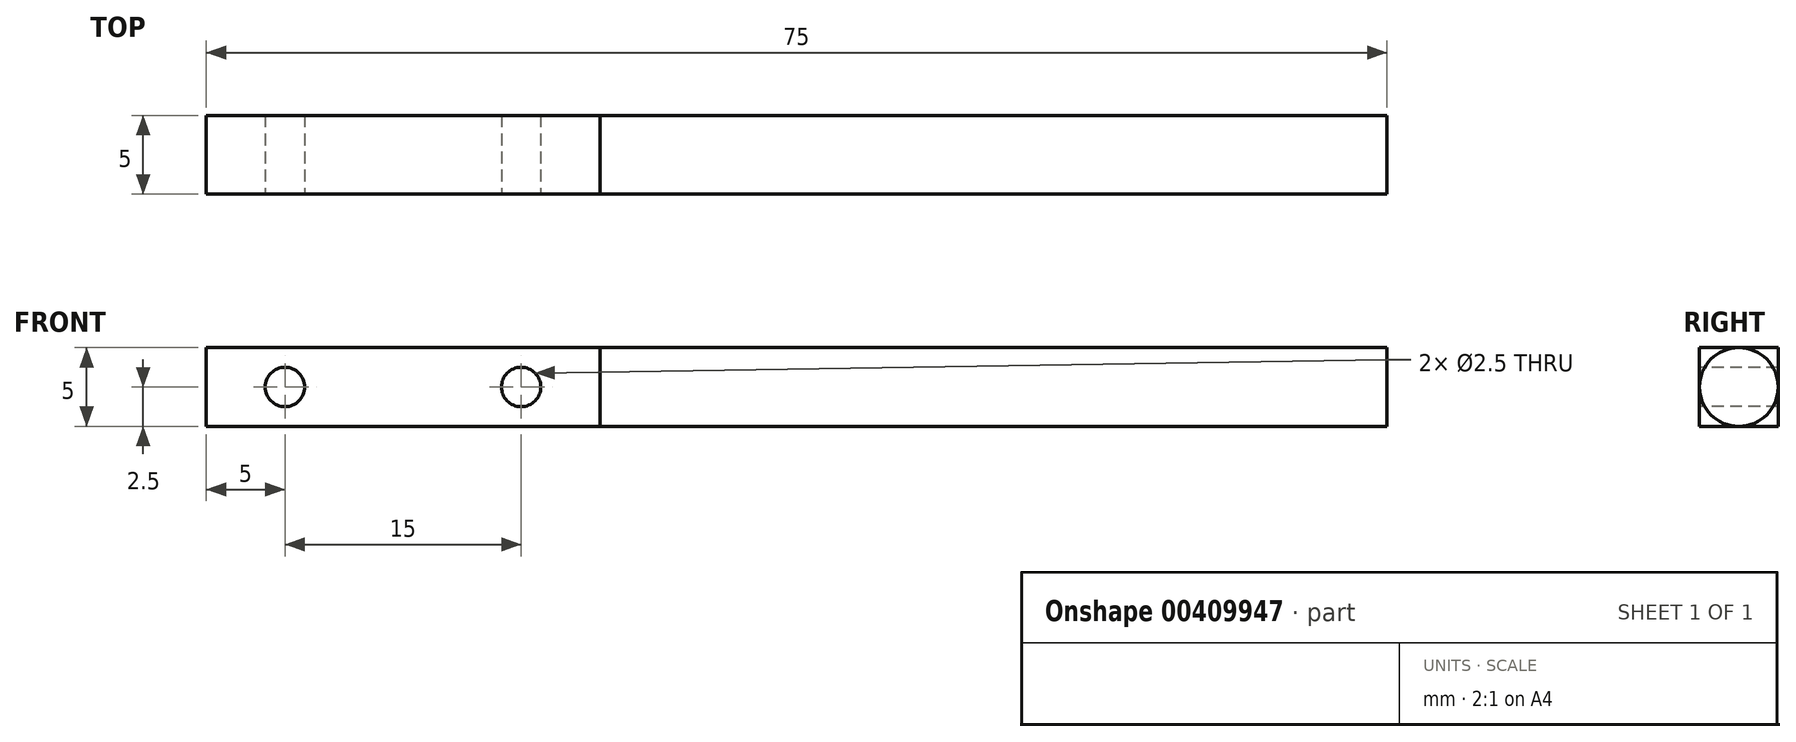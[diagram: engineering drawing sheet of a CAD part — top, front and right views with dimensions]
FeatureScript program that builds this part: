
annotation { "Feature Type Name" : "Feature", "Feature Type Description" : "" }
export const myFeature = defineFeature(function(context is Context, id is Id, definition is map)
    precondition{}
    {
        {
            var Q0;
            Q0=qCreatedBy(makeId("Right.planeOp"),FACE);
            var sketch = newSketch(context, id + "F0", { "sketchPlane" : qUnion([Q0])});
            skLineSegment(sketch, "E0.bottom", {"start": v(0, 0) * mm, "end": v(5, 0) * mm});
            skLineSegment(sketch, "E0.top", {"start": v(0, 5) * mm, "end": v(5, 5) * mm});
            skLineSegment(sketch, "E0.left", {"start": v(0, 0) * mm, "end": v(0, 5) * mm});
            skLineSegment(sketch, "E0.right", {"start": v(5, 0) * mm, "end": v(5, 5) * mm});
            skSolve(sketch);
        }
        {
            var Q0;
            Q0=makeQuery(id+"F0.imprint","IMPRINT",FACE,{"disambiguationData":[TD([[makeQuery(id+"F0.imprint","IMPRINT",EDGE,{"derivedFrom":sQuery(id+"F0.wireOp",EDGE,"E0.bottom")}),1.0]])]});
            extrude(context, id + "F1", {"entities" : qUnion([Q0]), "depth" : 25 * mm});
        }
        {
            var Q0;
            Q0=makeQuery(id+"F1.opExtrude","CAP_FACE",FACE,{"disambiguationData":[OSD([sQuery(id+"F0.wireOp",EDGE,"E0.bottom"),sQuery(id+"F0.wireOp",EDGE,"E0.top"),sQuery(id+"F0.wireOp",EDGE,"E0.left"),sQuery(id+"F0.wireOp",EDGE,"E0.right")])],"isStart":false});
            var sketch = newSketch(context, id + "F2", { "sketchPlane" : qUnion([Q0])});
            skCircle(sketch, "E1", {"center": v(2.5, 2.5) * mm, "radius": 2.5 * mm});
            skSolve(sketch);
        }
        {
            var Q0;
            {var subQ0=sQuery(id+"F2.wireOp",EDGE,"E1");var subQ1=makeQuery(id+"F2.imprint","INTERSECT",VERTEX,{"derivedFrom":[makeQuery(id+"F1.opExtrude","CAP_EDGE",EDGE,{"disambiguationData":[OSD([sQuery(id+"F0.wireOp",EDGE,"E0.top")])],"isStart":false}),subQ0]});Q0=makeQuery(id+"F2.imprint","IMPRINT",FACE,{"disambiguationData":[TD([[makeQuery(id+"F2.imprint","IMPRINT",EDGE,{"disambiguationData":[TD([[subQ1,1.0]])],"derivedFrom":subQ0}),1.0]])]});}
            extrude(context, id + "F3", {"entities" : qUnion([Q0]), "operationType" : NewBodyOperationType.ADD, "depth" : 50 * mm});
        }
        {
            var Q0;
            Q0=makeQuery(id+"F1.opExtrude","SWEPT_FACE",FACE,{"disambiguationData":[OSD([sQuery(id+"F0.wireOp",EDGE,"E0.left")])]});
            var sketch = newSketch(context, id + "F4", { "sketchPlane" : qUnion([Q0])});
            skCircle(sketch, "E2", {"center": v(5, 2.5) * mm, "radius": 1.25 * mm});
            skCircle(sketch, "E3", {"center": v(20, 2.5) * mm, "radius": 1.25 * mm});
            skSolve(sketch);
        }
        {
            var Q0;
            Q0=makeQuery(id+"F4.imprint","IMPRINT",FACE,{"disambiguationData":[TD([[makeQuery(id+"F4.imprint","IMPRINT",EDGE,{"derivedFrom":sQuery(id+"F4.wireOp",EDGE,"E2")}),1.0]])]});
            var Q1;
            Q1=makeQuery(id+"F4.imprint","IMPRINT",FACE,{"disambiguationData":[TD([[makeQuery(id+"F4.imprint","IMPRINT",EDGE,{"derivedFrom":sQuery(id+"F4.wireOp",EDGE,"E3")}),1.0]])]});
            extrude(context, id + "F5", {"entities" : qUnion([Q0, Q1]), "operationType" : NewBodyOperationType.REMOVE, "oppositeDirection" : true, "depth" : 25 * mm});
        }
    });
